# Revit family: Construction_Roof-Accessories_Alpine-SnowGuards_PP125
name_source: partatom
category: Specialty Equipment
units: mm (PartAtom-declared; Revit-internal decimal feet)

## family parameters
Cut with Voids When Loaded = No
Host = Face
OmniClass Number = 23.35.20.31.27.14
OmniClass Title = Snow Guards
Part Type = Normal
Room Calculation Point = No
Round Connector Dimension = Use Diameter
Shared = No

## types (3) — shared parameters
Assembly Code = B3010
Base Material = Alpine SnowGuards - Aluminium - Mill Finish
Default Elevation = 48"
Description = PP125 two or three pipe, pipe-style snow guard bracket. Multiple base plate sizes available.
Edition number = 1
Horizontal Spacing = 20"
Keynote = 07720
Manufacturer = Alpine SnowGuards
Pad Material = Alpine SnowGuards - Aluminium - Mill Finish
Product Guid = 183d45e3-ab5a-41be-a8dc-9c0c1bbc698b
Product Material = Alpine SnowGuards - Aluminium - Mill Finish
Product data url = https://www.bimobject.com
URL = https://www.alpinesnowguards.com
Z_Radius = 1/2"

## per-type parameters (varying)
| type | Model | Z_Hi Hole | Z_Three Pipe | Z_Two Pipe |
| Two Pipe | PP125 - Two Pipe | No | No | Yes |
| Three Pipe | PP125 - Three Pipe | No | Yes | No |
| Hi Hole | PP125 - Hi Hole | Yes | No | No |

## geometry (parser evidence)
native form markers: Sweep x9
no freeform markers — native parametric forms only
